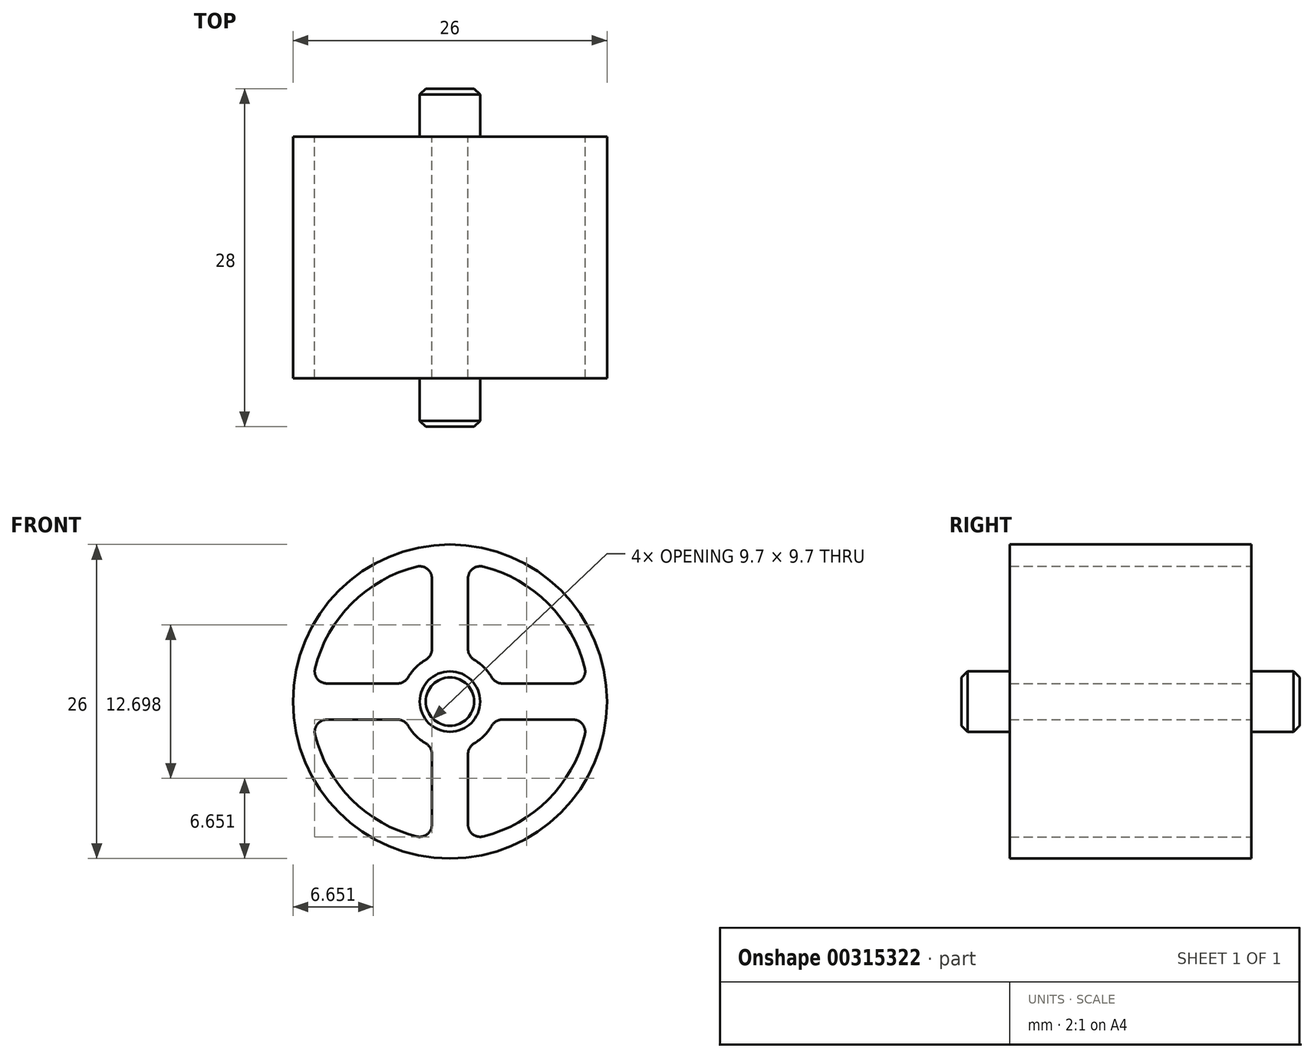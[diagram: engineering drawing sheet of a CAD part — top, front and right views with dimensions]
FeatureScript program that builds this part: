
annotation { "Feature Type Name" : "Feature", "Feature Type Description" : "" }
export const myFeature = defineFeature(function(context is Context, id is Id, definition is map)
    precondition{}
    {
        {
            var Q0;
            Q0=qCreatedBy(makeId("Front.planeOp"),FACE);
            var sketch = newSketch(context, id + "F0", { "sketchPlane" : qUnion([Q0])});
            skCircle(sketch, "E0", {"center": v(0, 0) * mm, "radius": 13 * mm});
            skArc(sketch, "E1", {"start": v(-11.17, -2.74) * mm, "mid": v(-8.13, -8.13) * mm, "end": v(-2.74, -11.17) * mm});
            skArc(sketch, "E2", {"start": v(-2, 3.46) * mm, "mid": v(-2.83, 2.83) * mm, "end": v(-3.46, 2) * mm});
            skLineSegment(sketch, "E3", {"start": v(-1.5, 10.2) * mm, "end": v(-1.5, 4.33) * mm});
            skLineSegment(sketch, "E4.trimOffspring", {"start": v(1.5, 10.2) * mm, "end": v(1.5, 4.33) * mm});
            skLineSegment(sketch, "E5", {"start": v(-1.5, -4.33) * mm, "end": v(-1.5, -10.2) * mm});
            skLineSegment(sketch, "E6", {"start": v(1.5, -4.33) * mm, "end": v(1.5, -10.2) * mm});
            skLineSegment(sketch, "E7", {"start": v(-4.33, 1.5) * mm, "end": v(-10.2, 1.5) * mm});
            skLineSegment(sketch, "E8", {"start": v(-4.33, -1.5) * mm, "end": v(-10.2, -1.5) * mm});
            skLineSegment(sketch, "E9", {"start": v(4.33, 1.5) * mm, "end": v(10.2, 1.5) * mm});
            skLineSegment(sketch, "E10", {"start": v(4.33, -1.5) * mm, "end": v(10.2, -1.5) * mm});
            skArc(sketch, "E11.trimOffspring", {"start": v(-2.74, 11.17) * mm, "mid": v(-8.13, 8.13) * mm, "end": v(-11.17, 2.74) * mm});
            skArc(sketch, "E12.trimOffspring", {"start": v(11.17, 2.74) * mm, "mid": v(8.13, 8.13) * mm, "end": v(2.74, 11.17) * mm});
            skArc(sketch, "E13.trimOffspring", {"start": v(2.74, -11.17) * mm, "mid": v(8.13, -8.13) * mm, "end": v(11.17, -2.74) * mm});
            skArc(sketch, "E14.trimOffspring", {"start": v(-3.46, -2) * mm, "mid": v(-2.83, -2.83) * mm, "end": v(-2, -3.46) * mm});
            skArc(sketch, "E15.trimOffspring", {"start": v(2, -3.46) * mm, "mid": v(2.83, -2.83) * mm, "end": v(3.46, -2) * mm});
            skArc(sketch, "E16.trimOffspring", {"start": v(3.46, 2) * mm, "mid": v(2.83, 2.83) * mm, "end": v(2, 3.46) * mm});
            skPoint(sketch, "E17.visualSharp", {"position": v(1.5, 11.4) * mm});
            skArc(sketch, "E17.filletArc", {"start": v(2.74, 11.17) * mm, "mid": v(1.88, 10.98) * mm, "end": v(1.5, 10.2) * mm});
            skPoint(sketch, "E18.visualSharp", {"position": v(-1.5, 11.4) * mm});
            skArc(sketch, "E18.filletArc", {"start": v(-1.5, 10.2) * mm, "mid": v(-1.88, 10.98) * mm, "end": v(-2.74, 11.17) * mm});
            skPoint(sketch, "E19.visualSharp", {"position": v(-11.4, 1.5) * mm});
            skArc(sketch, "E19.filletArc", {"start": v(-11.17, 2.74) * mm, "mid": v(-10.98, 1.88) * mm, "end": v(-10.2, 1.5) * mm});
            skPoint(sketch, "E20.visualSharp", {"position": v(-11.4, -1.5) * mm});
            skArc(sketch, "E20.filletArc", {"start": v(-10.2, -1.5) * mm, "mid": v(-10.98, -1.88) * mm, "end": v(-11.17, -2.74) * mm});
            skPoint(sketch, "E21.visualSharp", {"position": v(-1.5, -11.4) * mm});
            skArc(sketch, "E21.filletArc", {"start": v(-2.74, -11.17) * mm, "mid": v(-1.88, -10.98) * mm, "end": v(-1.5, -10.2) * mm});
            skPoint(sketch, "E22.visualSharp", {"position": v(1.5, -11.4) * mm});
            skArc(sketch, "E22.filletArc", {"start": v(1.5, -10.2) * mm, "mid": v(1.88, -10.98) * mm, "end": v(2.74, -11.17) * mm});
            skPoint(sketch, "E23.visualSharp", {"position": v(11.4, -1.5) * mm});
            skArc(sketch, "E23.filletArc", {"start": v(11.17, -2.74) * mm, "mid": v(10.98, -1.88) * mm, "end": v(10.2, -1.5) * mm});
            skPoint(sketch, "E24.visualSharp", {"position": v(11.4, 1.5) * mm});
            skArc(sketch, "E24.filletArc", {"start": v(10.2, 1.5) * mm, "mid": v(10.98, 1.88) * mm, "end": v(11.17, 2.74) * mm});
            skPoint(sketch, "E25.visualSharp", {"position": v(1.5, -3.7) * mm});
            skArc(sketch, "E25.filletArc", {"start": v(2, -3.46) * mm, "mid": v(1.63, -3.83) * mm, "end": v(1.5, -4.33) * mm});
            skPoint(sketch, "E26.visualSharp", {"position": v(3.7, -1.5) * mm});
            skArc(sketch, "E26.filletArc", {"start": v(4.33, -1.5) * mm, "mid": v(3.83, -1.63) * mm, "end": v(3.46, -2) * mm});
            skPoint(sketch, "E27.visualSharp", {"position": v(3.7, 1.5) * mm});
            skArc(sketch, "E27.filletArc", {"start": v(3.46, 2) * mm, "mid": v(3.83, 1.63) * mm, "end": v(4.33, 1.5) * mm});
            skPoint(sketch, "E28.visualSharp", {"position": v(1.5, 3.7) * mm});
            skArc(sketch, "E28.filletArc", {"start": v(1.5, 4.33) * mm, "mid": v(1.63, 3.83) * mm, "end": v(2, 3.46) * mm});
            skPoint(sketch, "E29.visualSharp", {"position": v(-1.5, 3.7) * mm});
            skArc(sketch, "E29.filletArc", {"start": v(-2, 3.46) * mm, "mid": v(-1.63, 3.83) * mm, "end": v(-1.5, 4.33) * mm});
            skPoint(sketch, "E30.visualSharp", {"position": v(-3.7, 1.5) * mm});
            skArc(sketch, "E30.filletArc", {"start": v(-4.33, 1.5) * mm, "mid": v(-3.83, 1.63) * mm, "end": v(-3.46, 2) * mm});
            skPoint(sketch, "E31.visualSharp", {"position": v(-3.7, -1.5) * mm});
            skArc(sketch, "E31.filletArc", {"start": v(-3.46, -2) * mm, "mid": v(-3.83, -1.63) * mm, "end": v(-4.33, -1.5) * mm});
            skPoint(sketch, "E32.visualSharp", {"position": v(-1.5, -3.7) * mm});
            skArc(sketch, "E32.filletArc", {"start": v(-1.5, -4.33) * mm, "mid": v(-1.63, -3.83) * mm, "end": v(-2, -3.46) * mm});
            skSolve(sketch);
        }
        {
            var Q0;
            Q0=makeQuery(id+"F0.imprint","IMPRINT",FACE,{"disambiguationData":[TD([[makeQuery(id+"F0.imprint","IMPRINT",EDGE,{"derivedFrom":sQuery(id+"F0.wireOp",EDGE,"E0")}),1.0]])]});
            extrude(context, id + "F1", {"entities" : qUnion([Q0]), "endBound" : BoundingType.SYMMETRIC, "depth" : 20 * mm});
        }
        {
            var Q0;
            Q0=qCreatedBy(makeId("Front.planeOp"),FACE);
            var sketch = newSketch(context, id + "F2", { "sketchPlane" : qUnion([Q0])});
            skCircle(sketch, "E33", {"center": v(0, 0) * mm, "radius": 2.5 * mm});
            skSolve(sketch);
        }
        {
            var Q0;
            Q0 = qSketchRegion(id + "F2", true);
            extrude(context, id + "F3", {"entities" : qUnion([Q0]), "operationType" : NewBodyOperationType.ADD, "endBound" : BoundingType.SYMMETRIC, "depth" : 28 * mm});
        }
        {
            var Q0;
            Q0=makeQuery(id+"F3.opExtrude","CAP_EDGE",EDGE,{"disambiguationData":[OSD([sQuery(id+"F2.wireOp",EDGE,"E33")])],"isStart":false});
            var Q1;
            Q1=makeQuery(id+"F3.opExtrude","CAP_EDGE",EDGE,{"disambiguationData":[OSD([sQuery(id+"F2.wireOp",EDGE,"E33")])],"isStart":true});
            chamfer(context, id + "F4", {"entities" : qUnion([Q0, Q1]), "width" : 0.5 * mm, "tangentPropagation" : true});
        }
    });
